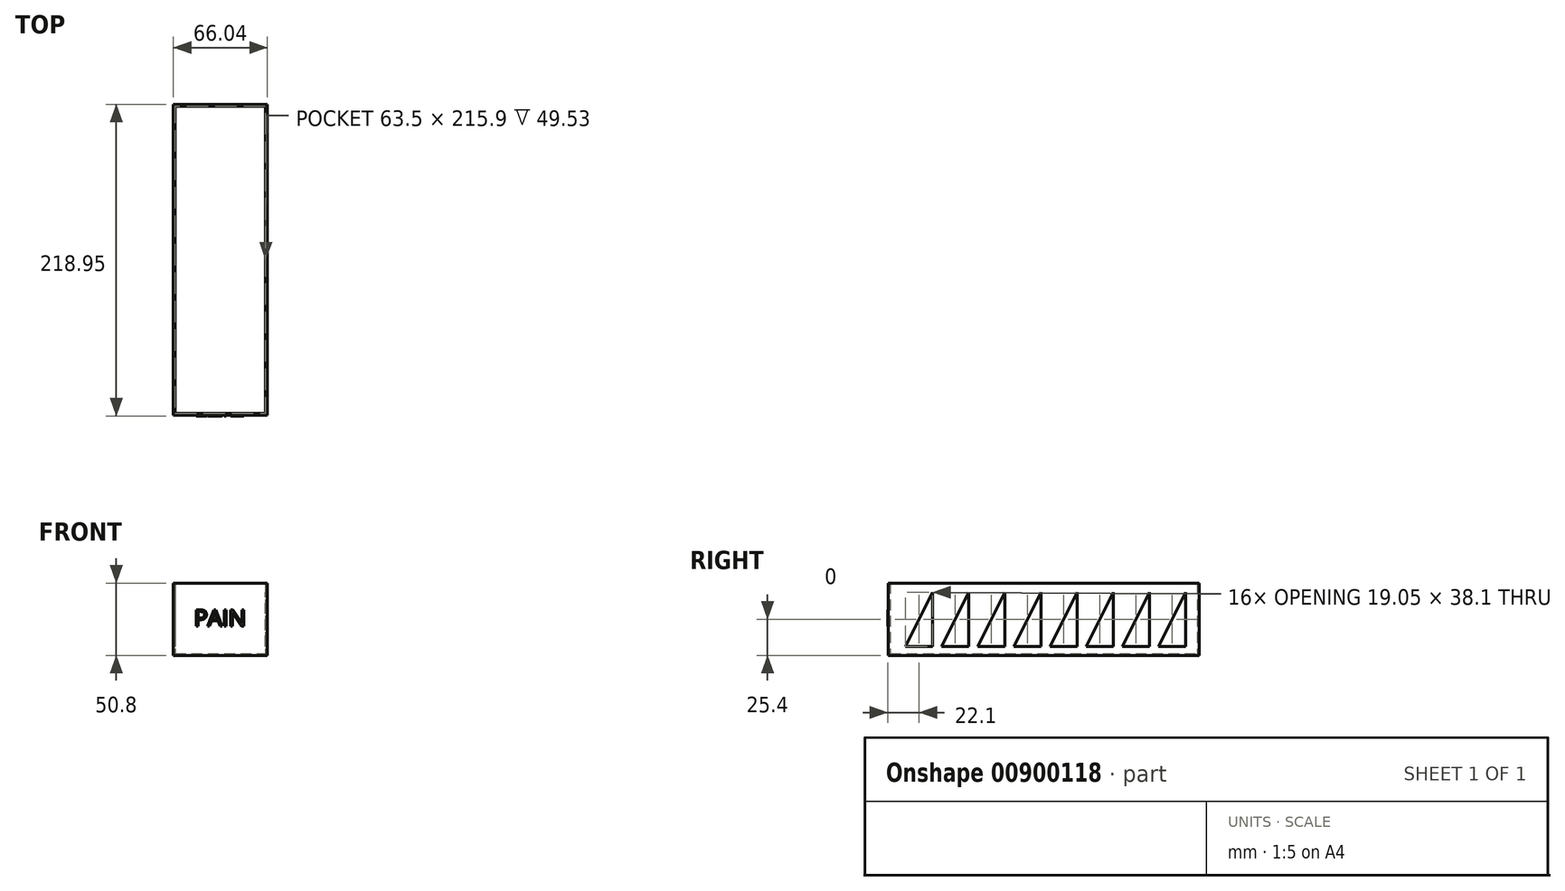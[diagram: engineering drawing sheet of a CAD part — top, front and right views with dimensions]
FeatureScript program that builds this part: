
annotation { "Feature Type Name" : "Feature", "Feature Type Description" : "" }
export const myFeature = defineFeature(function(context is Context, id is Id, definition is map)
    precondition{}
    {
        {
            var Q0;
            Q0=qCreatedBy(makeId("Top.planeOp"),FACE);
            var sketch = newSketch(context, id + "F0", { "sketchPlane" : qUnion([Q0])});
            skLineSegment(sketch, "E0.bottom", {"start": v(31.75, 107.95) * mm, "end": v(-31.75, 107.95) * mm});
            skLineSegment(sketch, "E0.top", {"start": v(31.75, -107.95) * mm, "end": v(-31.75, -107.95) * mm});
            skLineSegment(sketch, "E0.left", {"start": v(31.75, 107.95) * mm, "end": v(31.75, -107.95) * mm});
            skLineSegment(sketch, "E0.right", {"start": v(-31.75, 107.95) * mm, "end": v(-31.75, -107.95) * mm});
            skPoint(sketch, "E0.middle", {"position": v(0, 0) * mm});
            skLineSegment(sketch, "E1.0", {"start": v(33.02, 109.22) * mm, "end": v(-33.02, 109.22) * mm});
            skLineSegment(sketch, "E1.1", {"start": v(33.02, 109.22) * mm, "end": v(33.02, -109.22) * mm});
            skLineSegment(sketch, "E1.2", {"start": v(33.02, -109.22) * mm, "end": v(-33.02, -109.22) * mm});
            skLineSegment(sketch, "E1.3", {"start": v(-33.02, 109.22) * mm, "end": v(-33.02, -109.22) * mm});
            skSolve(sketch);
        }
        {
            var Q0;
            Q0 = qSketchRegion(id + "F0", true);
            var Q1;
            Q1=makeQuery(id+"F0.imprint","IMPRINT",FACE,{"disambiguationData":[TD([[makeQuery(id+"F0.imprint","IMPRINT",EDGE,{"derivedFrom":sQuery(id+"F0.wireOp",EDGE,"E0.bottom")}),1.0]])]});
            extrude(context, id + "F1", {"entities" : qUnion([Q0, Q1]), "depth" : 1.27 * mm, "offsetDistance" : 25.4 * mm});
        }
        {
            var Q0;
            Q0 = qSketchRegion(id + "F0", true);
            extrude(context, id + "F2", {"entities" : qUnion([Q0]), "operationType" : NewBodyOperationType.ADD, "depth" : 50.8 * mm, "offsetDistance" : 25.4 * mm});
        }
        {
            var Q0;
            {var subQ0=sQuery(id+"F0.wireOp",EDGE,"E1.3");Q0=makeQuery(id+"F2.boolean.opBoolean","MERGE",FACE,{"derivedFrom":[makeQuery(id+"F1.opExtrude","SWEPT_FACE",FACE,{"disambiguationData":[OSD([subQ0])]}),makeQuery(id+"F2.opExtrude","SWEPT_FACE",FACE,{"disambiguationData":[OSD([subQ0])]})]});}
            var sketch = newSketch(context, id + "F3", { "sketchPlane" : qUnion([Q0])});
            skLineSegment(sketch, "E2", {"start": v(-99.7, 44.45) * mm, "end": v(-99.7, 6.35) * mm});
            skLineSegment(sketch, "E3", {"start": v(-99.7, 6.35) * mm, "end": v(-80.65, 6.35) * mm});
            skLineSegment(sketch, "E4", {"start": v(-80.64, 6.35) * mm, "end": v(-99.7, 44.45) * mm});
            skLineSegment(sketch, "E5.1.0.0", {"start": v(-55.25, 6.35) * mm, "end": v(-74.3, 44.45) * mm});
            skLineSegment(sketch, "E5.1.0.1", {"start": v(-74.3, 44.45) * mm, "end": v(-74.3, 6.35) * mm});
            skLineSegment(sketch, "E5.1.0.2", {"start": v(-74.3, 44.45) * mm, "end": v(-74.3, 44.45) * mm});
            skLineSegment(sketch, "E5.1.0.3", {"start": v(-74.3, 6.35) * mm, "end": v(-55.25, 6.35) * mm});
            skLineSegment(sketch, "E5.2.0.0", {"start": v(-29.85, 6.35) * mm, "end": v(-48.9, 44.45) * mm});
            skLineSegment(sketch, "E5.2.0.1", {"start": v(-48.9, 44.45) * mm, "end": v(-48.9, 6.35) * mm});
            skLineSegment(sketch, "E5.2.0.2", {"start": v(-48.9, 44.45) * mm, "end": v(-48.9, 44.45) * mm});
            skLineSegment(sketch, "E5.2.0.3", {"start": v(-48.9, 6.35) * mm, "end": v(-29.85, 6.35) * mm});
            skLineSegment(sketch, "E5.3.0.0", {"start": v(-4.45, 6.35) * mm, "end": v(-23.5, 44.45) * mm});
            skLineSegment(sketch, "E5.3.0.1", {"start": v(-23.5, 44.45) * mm, "end": v(-23.5, 6.35) * mm});
            skLineSegment(sketch, "E5.3.0.2", {"start": v(-23.5, 44.45) * mm, "end": v(-23.5, 44.45) * mm});
            skLineSegment(sketch, "E5.3.0.3", {"start": v(-23.5, 6.35) * mm, "end": v(-4.45, 6.35) * mm});
            skLineSegment(sketch, "E5.4.0.0", {"start": v(20.95, 6.35) * mm, "end": v(1.9, 44.45) * mm});
            skLineSegment(sketch, "E5.4.0.1", {"start": v(1.9, 44.45) * mm, "end": v(1.9, 6.35) * mm});
            skLineSegment(sketch, "E5.4.0.2", {"start": v(1.9, 44.45) * mm, "end": v(1.9, 44.45) * mm});
            skLineSegment(sketch, "E5.4.0.3", {"start": v(1.9, 6.35) * mm, "end": v(20.95, 6.35) * mm});
            skLineSegment(sketch, "E5.5.0.0", {"start": v(46.35, 6.35) * mm, "end": v(27.3, 44.45) * mm});
            skLineSegment(sketch, "E5.5.0.1", {"start": v(27.3, 44.45) * mm, "end": v(27.3, 6.35) * mm});
            skLineSegment(sketch, "E5.5.0.2", {"start": v(27.3, 44.45) * mm, "end": v(27.3, 44.45) * mm});
            skLineSegment(sketch, "E5.5.0.3", {"start": v(27.3, 6.35) * mm, "end": v(46.35, 6.35) * mm});
            skLineSegment(sketch, "E5.6.0.0", {"start": v(71.75, 6.35) * mm, "end": v(52.7, 44.45) * mm});
            skLineSegment(sketch, "E5.6.0.1", {"start": v(52.7, 44.45) * mm, "end": v(52.7, 6.35) * mm});
            skLineSegment(sketch, "E5.6.0.2", {"start": v(52.7, 44.45) * mm, "end": v(52.7, 44.45) * mm});
            skLineSegment(sketch, "E5.6.0.3", {"start": v(52.7, 6.35) * mm, "end": v(71.75, 6.35) * mm});
            skLineSegment(sketch, "E5.7.0.0", {"start": v(97.15, 6.35) * mm, "end": v(78.1, 44.45) * mm});
            skLineSegment(sketch, "E5.7.0.1", {"start": v(78.1, 44.45) * mm, "end": v(78.1, 6.35) * mm});
            skLineSegment(sketch, "E5.7.0.2", {"start": v(78.1, 44.45) * mm, "end": v(78.1, 44.45) * mm});
            skLineSegment(sketch, "E5.7.0.3", {"start": v(78.1, 6.35) * mm, "end": v(97.15, 6.35) * mm});
            skLineSegment(sketch, "E5.direction1", {"start": v(-80.65, 6.35) * mm, "end": v(-55.25, 6.35) * mm, "construction": true});
            skSolve(sketch);
        }
        {
            var Q0;
            Q0 = qSketchRegion(id + "F3", true);
            extrude(context, id + "F4", {"entities" : qUnion([Q0]), "operationType" : NewBodyOperationType.REMOVE, "oppositeDirection" : true, "depth" : 76.2 * mm, "offsetDistance" : 25.4 * mm});
        }
        {
            var Q0;
            {var subQ0=sQuery(id+"F0.wireOp",EDGE,"E1.2");Q0=makeQuery(id+"F2.boolean.opBoolean","MERGE",FACE,{"derivedFrom":[makeQuery(id+"F1.opExtrude","SWEPT_FACE",FACE,{"disambiguationData":[OSD([subQ0])]}),makeQuery(id+"F2.opExtrude","SWEPT_FACE",FACE,{"disambiguationData":[OSD([subQ0])]})]});}
            var sketch = newSketch(context, id + "F5", { "sketchPlane" : qUnion([Q0])});
            skText(sketch, "E6", { "text": "PAIN", "fontName": "OpenSans-Regular.ttf"});
            const initialGuessF5  = {"E6": [-0.01858, 0.02057, 1, 0, 0.01157]};
            skSetInitialGuess(sketch, initialGuessF5);
            skSolve(sketch);
        }
        {
            var Q0;
            Q0 = qSketchRegion(id + "F5", true);
            extrude(context, id + "F6", {"entities" : qUnion([Q0]), "operationType" : NewBodyOperationType.ADD, "depth" : 0.5 * mm, "offsetDistance" : 25.4 * mm});
        }
    });
